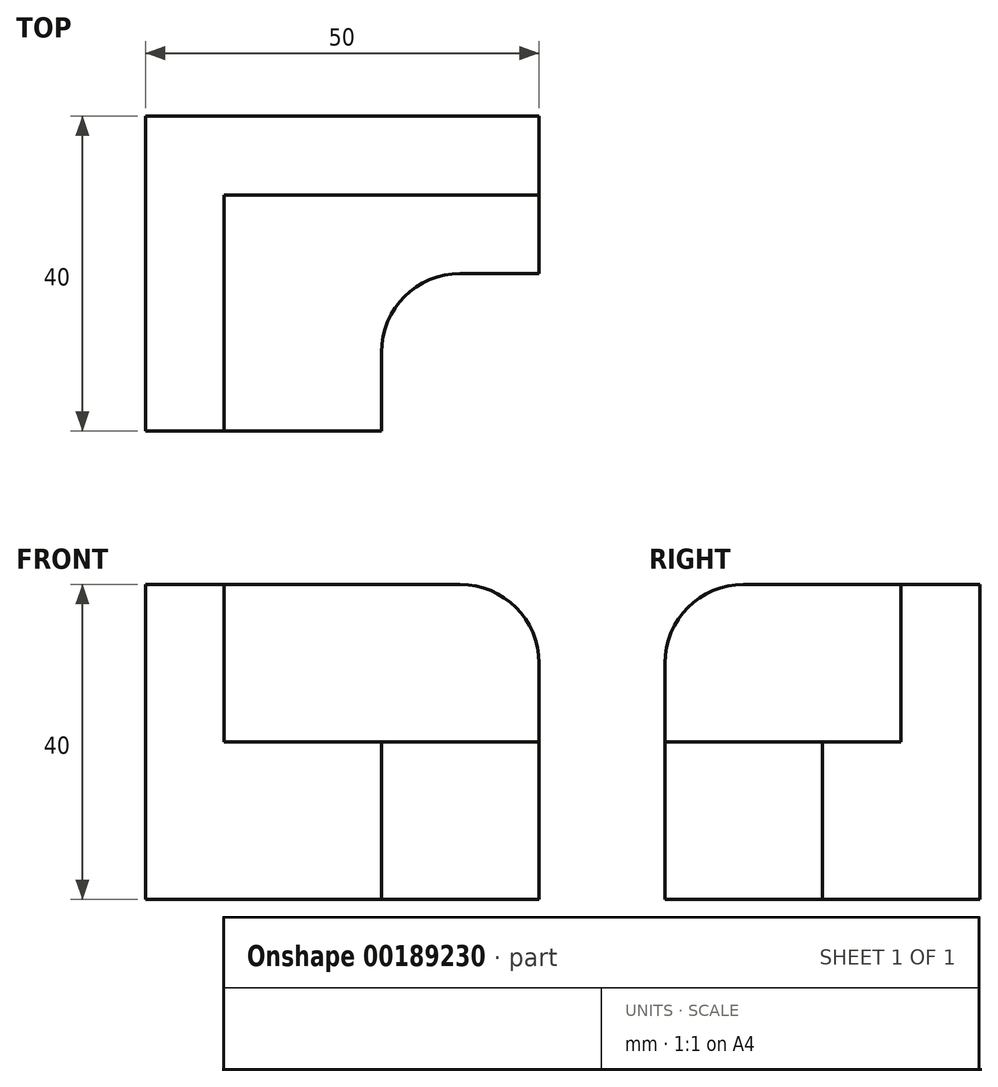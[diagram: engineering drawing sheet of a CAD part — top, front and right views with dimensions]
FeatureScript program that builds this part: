
annotation { "Feature Type Name" : "Feature", "Feature Type Description" : "" }
export const myFeature = defineFeature(function(context is Context, id is Id, definition is map)
    precondition{}
    {
        {
            var Q0;
            Q0=qCreatedBy(makeId("Top.planeOp"),FACE);
            var sketch = newSketch(context, id + "F0", { "sketchPlane" : qUnion([Q0])});
            skLineSegment(sketch, "E0.bottom", {"start": v(0, 0) * mm, "end": v(30, 0) * mm});
            skLineSegment(sketch, "E0.top", {"start": v(0, 40) * mm, "end": v(50, 40) * mm});
            skLineSegment(sketch, "E0.left", {"start": v(0, 0) * mm, "end": v(0, 40) * mm});
            skLineSegment(sketch, "E0.right", {"start": v(50, 20) * mm, "end": v(50, 40) * mm});
            skLineSegment(sketch, "E1", {"start": v(30, 0) * mm, "end": v(30, 10) * mm});
            skPoint(sketch, "E1.endSnap0", {"position": v(50, 20) * mm});
            skLineSegment(sketch, "E2", {"start": v(40, 20) * mm, "end": v(50, 20) * mm});
            skPoint(sketch, "E3.orphan", {"position": v(50, 0) * mm});
            skPoint(sketch, "E4.visualSharp", {"position": v(30, 20) * mm});
            skArc(sketch, "E4.filletArc", {"start": v(40, 20) * mm, "mid": v(32.93, 17.07) * mm, "end": v(30, 10) * mm});
            skSolve(sketch);
        }
        {
            var Q0;
            Q0=makeQuery(id+"F0.imprint","IMPRINT",FACE,{"disambiguationData":[TD([[makeQuery(id+"F0.imprint","IMPRINT",EDGE,{"derivedFrom":sQuery(id+"F0.wireOp",EDGE,"E0.bottom")}),1.0]])]});
            extrude(context, id + "F1", {"entities" : qUnion([Q0]), "depth" : 40 * mm});
        }
        {
            var Q0;
            Q0=makeQuery(id+"F1.opExtrude","CAP_FACE",FACE,{"disambiguationData":[OSD([sQuery(id+"F0.wireOp",EDGE,"E0.bottom"),sQuery(id+"F0.wireOp",EDGE,"E0.top"),sQuery(id+"F0.wireOp",EDGE,"E0.left"),sQuery(id+"F0.wireOp",EDGE,"E0.right"),sQuery(id+"F0.wireOp",EDGE,"E1"),sQuery(id+"F0.wireOp",EDGE,"E2"),sQuery(id+"F0.wireOp",EDGE,"E4.filletArc")])],"isStart":false});
            var sketch = newSketch(context, id + "F2", { "sketchPlane" : qUnion([Q0])});
            skLineSegment(sketch, "E5", {"start": v(50, 30) * mm, "end": v(10, 30) * mm});
            skLineSegment(sketch, "E6", {"start": v(10, 30) * mm, "end": v(10, 0) * mm});
            skPoint(sketch, "E7.orphan", {"position": v(30, 0) * mm});
            skPoint(sketch, "E8.orphan", {"position": v(50, 20) * mm});
            skLineSegment(sketch, "E9.0", {"start": v(10, 0) * mm, "end": v(30, 0) * mm});
            skLineSegment(sketch, "E10.0", {"start": v(30, 0) * mm, "end": v(30, 10) * mm});
            skArc(sketch, "E11.0", {"start": v(40, 20) * mm, "mid": v(32.93, 17.07) * mm, "end": v(30, 10) * mm});
            skLineSegment(sketch, "E12.0", {"start": v(40, 20) * mm, "end": v(50, 20) * mm});
            skLineSegment(sketch, "E13.0", {"start": v(50, 20) * mm, "end": v(50, 30) * mm});
            skPoint(sketch, "E14.orphan", {"position": v(0, 0) * mm});
            skPoint(sketch, "E15.orphan", {"position": v(50, 40) * mm});
            skSolve(sketch);
        }
        {
            var Q0;
            Q0=makeQuery(id+"F2.imprint","IMPRINT",FACE,{"disambiguationData":[TD([[makeQuery(id+"F2.imprint","IMPRINT",EDGE,{"derivedFrom":sQuery(id+"F2.wireOp",EDGE,"E5")}),1.0]])]});
            extrude(context, id + "F3", {"entities" : qUnion([Q0]), "operationType" : NewBodyOperationType.REMOVE, "oppositeDirection" : true, "depth" : 20 * mm});
        }
        {
            var Q0;
            Q0=makeQuery(id+"F1.opExtrude","CAP_EDGE",EDGE,{"disambiguationData":[OSD([sQuery(id+"F0.wireOp",EDGE,"E0.right")])],"isStart":false});
            var Q1;
            Q1=makeQuery(id+"F1.opExtrude","CAP_EDGE",EDGE,{"disambiguationData":[OSD([sQuery(id+"F0.wireOp",EDGE,"E0.bottom")])],"isStart":false});
            fillet(context, id + "F4", {"entities" : qUnion([Q0, Q1]), "radius" : 10 * mm, "tangentPropagation" : true, "allowEdgeOverflow" : false});
        }
    });
